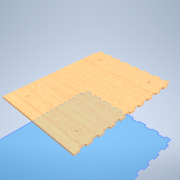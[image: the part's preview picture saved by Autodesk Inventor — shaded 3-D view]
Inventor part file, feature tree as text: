
AUTODESK INVENTOR PART (.ipt)
format: ipt  version: 2021 (Build 250183000, 183)  size: 254,464 bytes
history: native  units: mm
features: extrude x3, sketch x2, other x1
ambient origin geometry x8: Origin, YZ Plane, XZ Plane, XY Plane, X Axis, Y Axis, Z Axis, Center Point
bodies: Body1 (feature_tree)
feature tree (6):
  other  "DoosjeOnderkant"
  extrude  "Extrusion2"  Depth=200.0mm
  extrude  "Extrusion3"  Depth=90.0mm
  extrude  "Extrusion4"  Depth=3.0mm TaperAngle=0.0deg
  sketch  "Sketch3"  dims[d4=150.0mm d5=200.0mm]
  sketch  "Sketch5"  dims[d6=3.0mm d7=0.0mm d21=90.0mm d23=20.0mm d24=10.0mm d26=10.0mm d29=3.0mm d30=0.0mm d38=5.0mm d39=100.0mm d40=150.0mm d41=2.0mm d42=0.0mm d2=0.5mm d3=0.872665mm]
